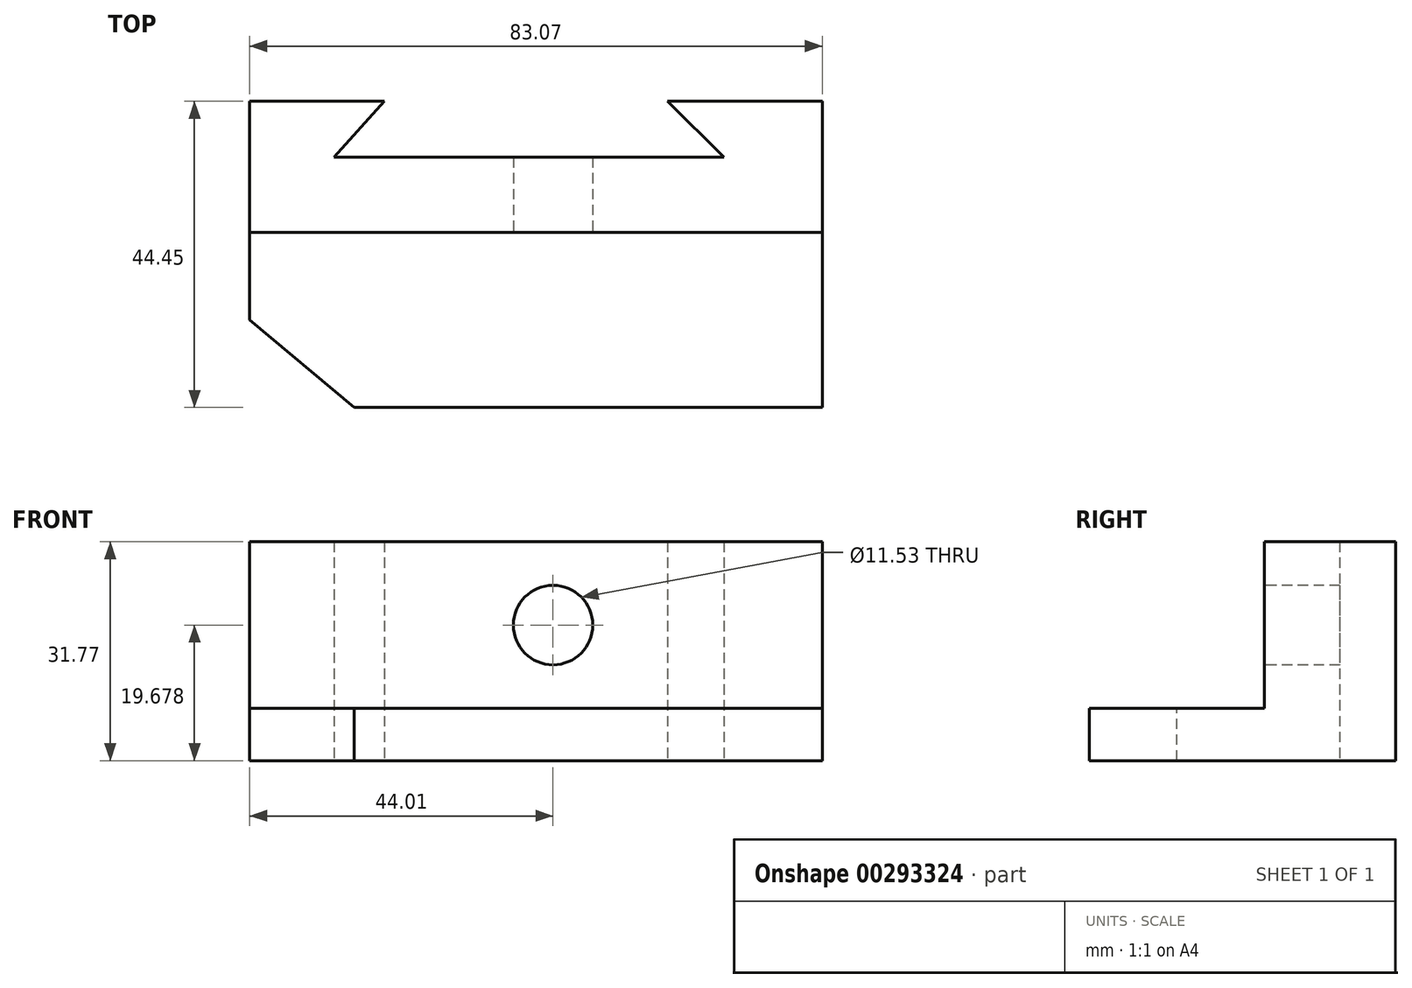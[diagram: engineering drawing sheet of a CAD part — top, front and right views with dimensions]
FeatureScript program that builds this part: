
annotation { "Feature Type Name" : "Feature", "Feature Type Description" : "" }
export const myFeature = defineFeature(function(context is Context, id is Id, definition is map)
    precondition{}
    {
        {
            var Q0;
            Q0=qCreatedBy(makeId("Front.planeOp"),FACE);
            var sketch = newSketch(context, id + "F0", { "sketchPlane" : qUnion([Q0])});
            skLineSegment(sketch, "E0", {"start": v(-44.01, 43.28) * mm, "end": v(-44.01, 11.51) * mm});
            skLineSegment(sketch, "E1", {"start": v(-44.01, 11.51) * mm, "end": v(39.06, 11.51) * mm});
            skLineSegment(sketch, "E2", {"start": v(39.06, 11.51) * mm, "end": v(39.06, 43.28) * mm});
            skLineSegment(sketch, "E3", {"start": v(39.06, 43.28) * mm, "end": v(-44.01, 43.28) * mm});
            skSolve(sketch);
        }
        {
            var Q0;
            Q0 = qSketchRegion(id + "F0", true);
            extrude(context, id + "F1", {"entities" : qUnion([Q0]), "oppositeDirection" : true, "depth" : 19.05 * mm});
        }
        {
            var Q0;
            Q0=makeQuery(id+"F1.opExtrude","SWEPT_FACE",FACE,{"disambiguationData":[OSD([sQuery(id+"F0.wireOp",EDGE,"E1")])]});
            var sketch = newSketch(context, id + "F2", { "sketchPlane" : qUnion([Q0])});
            skLineSegment(sketch, "E4", {"start": v(-24.48, -19.05) * mm, "end": v(-31.77, -10.93) * mm});
            skLineSegment(sketch, "E5", {"start": v(-31.77, -10.93) * mm, "end": v(24.78, -10.93) * mm});
            skLineSegment(sketch, "E6", {"start": v(24.78, -10.93) * mm, "end": v(16.61, -19.05) * mm});
            skSolve(sketch);
        }
        {
            var Q0;
            {var subQ0=sQuery(id+"F2.wireOp",EDGE,"E4");Q0=makeQuery(id+"F2.imprint","IMPRINT",FACE,{"disambiguationData":[TD([[makeQuery(id+"F2.imprint","IMPRINT",EDGE,{"derivedFrom":subQ0}),-1.0]])]});}
            extrude(context, id + "F3", {"entities" : qUnion([Q0]), "operationType" : NewBodyOperationType.REMOVE, "oppositeDirection" : true, "depth" : 35.05 * mm});
        }
        {
            var Q0;
            Q0=makeQuery(id+"F1.opExtrude","CAP_FACE",FACE,{"disambiguationData":[OSD([sQuery(id+"F0.wireOp",EDGE,"E0"),sQuery(id+"F0.wireOp",EDGE,"E1"),sQuery(id+"F0.wireOp",EDGE,"E2"),sQuery(id+"F0.wireOp",EDGE,"E3")])],"isStart":true});
            var sketch = newSketch(context, id + "F4", { "sketchPlane" : qUnion([Q0])});
            skLineSegment(sketch, "E7", {"start": v(39.06, 19.1) * mm, "end": v(-44.01, 19.1) * mm});
            skSolve(sketch);
        }
        {
            var Q0;
            Q0 = qSketchRegion(id + "F4", true);
            var Q1;
            {var subQ0=sQuery(id+"F4.wireOp",EDGE,"E7");Q1=makeQuery(id+"F4.imprint","IMPRINT",FACE,{"disambiguationData":[TD([[makeQuery(id+"F4.imprint","IMPRINT",EDGE,{"derivedFrom":subQ0}),1.0]])]});}
            extrude(context, id + "F5", {"entities" : qUnion([Q0, Q1]), "operationType" : NewBodyOperationType.ADD, "depth" : 25.4 * mm});
        }
        {
            var Q0;
            Q0=makeQuery(id+"F5.opExtrude","SWEPT_FACE",FACE,{"disambiguationData":[OSD([sQuery(id+"F4.wireOp",EDGE,"E7")])]});
            var sketch = newSketch(context, id + "F6", { "sketchPlane" : qUnion([Q0])});
            skLineSegment(sketch, "E8", {"start": v(39.06, -12.7) * mm, "end": v(23.9, -25.4) * mm});
            skLineSegment(sketch, "E9", {"start": v(23.9, -25.4) * mm, "end": v(39.06, -12.7) * mm});
            skLineSegment(sketch, "E10", {"start": v(-44.01, -12.7) * mm, "end": v(-28.86, -25.4) * mm});
            skSolve(sketch);
        }
        {
            var Q0;
            Q0 = qSketchRegion(id + "F6", true);
            var Q1;
            {var subQ0=sQuery(id+"F6.wireOp",EDGE,"E9");Q1=makeQuery(id+"F6.imprint","IMPRINT",FACE,{"disambiguationData":[TD([[makeQuery(id+"F6.imprint","IMPRINT",EDGE,{"derivedFrom":subQ0}),-1.0]])]});}
            var Q2;
            {var subQ0=sQuery(id+"F6.wireOp",EDGE,"E10");Q2=makeQuery(id+"F6.imprint","IMPRINT",FACE,{"disambiguationData":[TD([[makeQuery(id+"F6.imprint","IMPRINT",EDGE,{"derivedFrom":subQ0}),-1.0]])]});}
            extrude(context, id + "F7", {"entities" : qUnion([Q0, Q1, Q2]), "operationType" : NewBodyOperationType.REMOVE, "oppositeDirection" : true, "depth" : 25.4 * mm});
        }
        {
            var Q0;
            Q0=makeQuery(id+"F1.opExtrude","CAP_FACE",FACE,{"disambiguationData":[OSD([sQuery(id+"F0.wireOp",EDGE,"E0"),sQuery(id+"F0.wireOp",EDGE,"E1"),sQuery(id+"F0.wireOp",EDGE,"E2"),sQuery(id+"F0.wireOp",EDGE,"E3")])],"isStart":true});
            var sketch = newSketch(context, id + "F8", { "sketchPlane" : qUnion([Q0])});
            skCircle(sketch, "E11", {"center": v(0, 31.19) * mm, "radius": 5.77 * mm});
            skPoint(sketch, "E11.centerSnap0", {"position": v(39.06, 31.19) * mm});
            skSolve(sketch);
        }
        {
            var Q0;
            Q0 = qSketchRegion(id + "F8", true);
            extrude(context, id + "F9", {"entities" : qUnion([Q0]), "operationType" : NewBodyOperationType.REMOVE, "oppositeDirection" : true, "depth" : 25.4 * mm});
        }
    });
